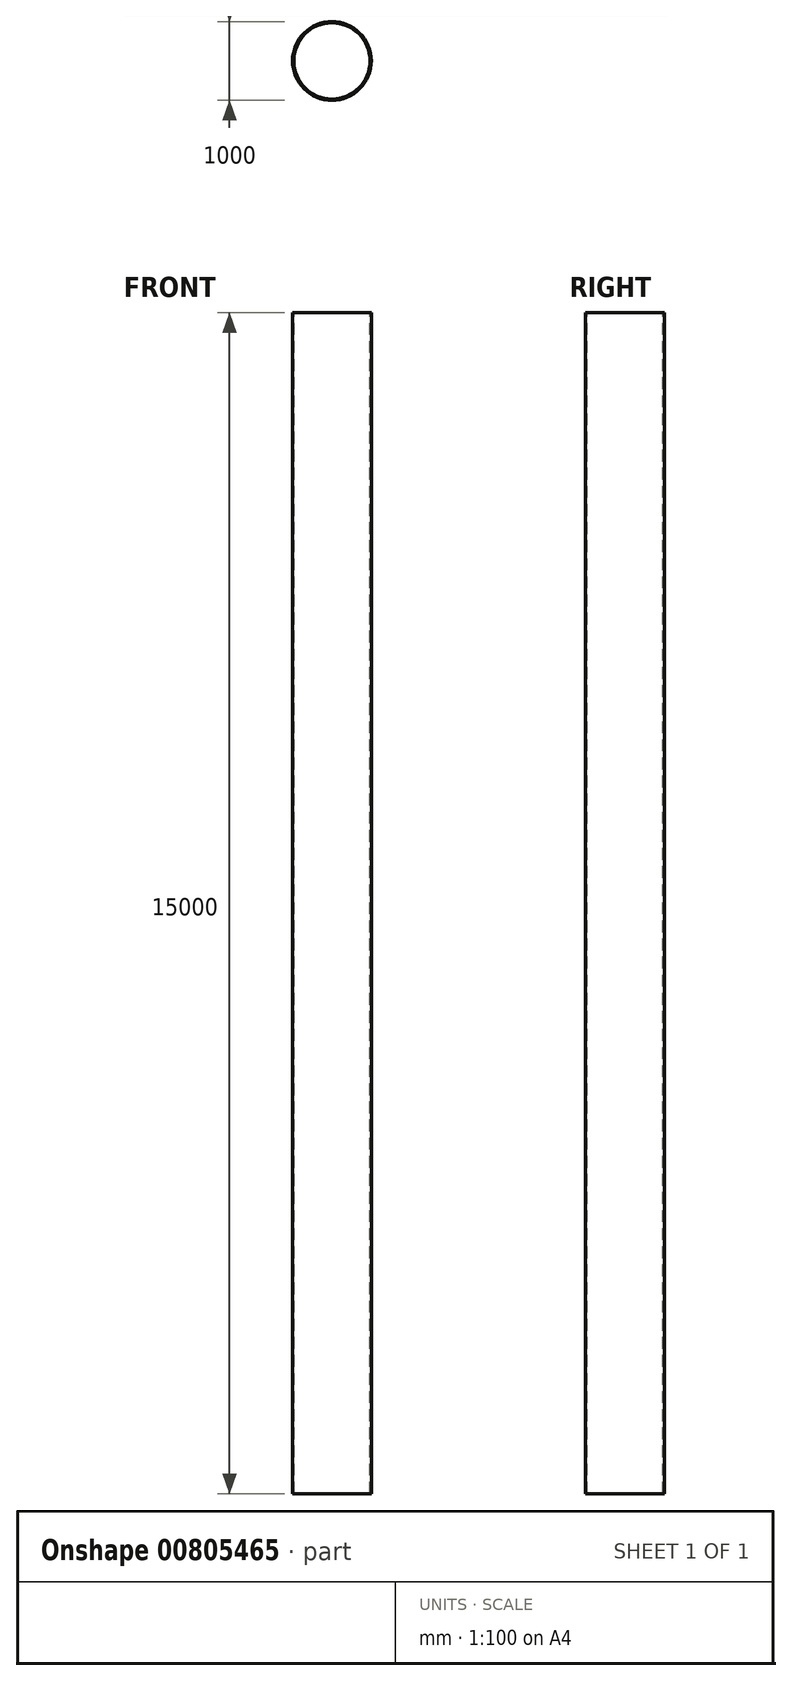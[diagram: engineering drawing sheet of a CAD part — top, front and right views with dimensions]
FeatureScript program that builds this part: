
annotation { "Feature Type Name" : "Feature", "Feature Type Description" : "" }
export const myFeature = defineFeature(function(context is Context, id is Id, definition is map)
    precondition{}
    {
        {
            var Q0;
            Q0=qCreatedBy(makeId("Top.planeOp"),FACE);
            var sketch = newSketch(context, id + "F0", { "sketchPlane" : qUnion([Q0])});
            skCircle(sketch, "E0", {"center": v(0, 0) * mm, "radius": 500 * mm});
            skSolve(sketch);
        }
        {
            var Q0;
            Q0 = qSketchRegion(id + "F0", true);
            extrude(context, id + "F1", {"entities" : qUnion([Q0]), "oppositeDirection" : true, "depth" : 15000 * mm, "offsetDistance" : 25 * mm});
        }
        {
            var Q0;
            Q0=qCreatedBy(makeId("Top.planeOp"),FACE);
            var sketch = newSketch(context, id + "F2", { "sketchPlane" : qUnion([Q0])});
            skCircle(sketch, "E1", {"center": v(0, 0) * mm, "radius": 484 * mm});
            skSolve(sketch);
        }
        {
            var Q0;
            Q0 = qSketchRegion(id + "F2", true);
            extrude(context, id + "F3", {"entities" : qUnion([Q0]), "operationType" : NewBodyOperationType.REMOVE, "endBound" : BoundingType.THROUGH_ALL, "oppositeDirection" : true, "depth" : 25 * mm, "offsetDistance" : 25 * mm});
        }
    });
